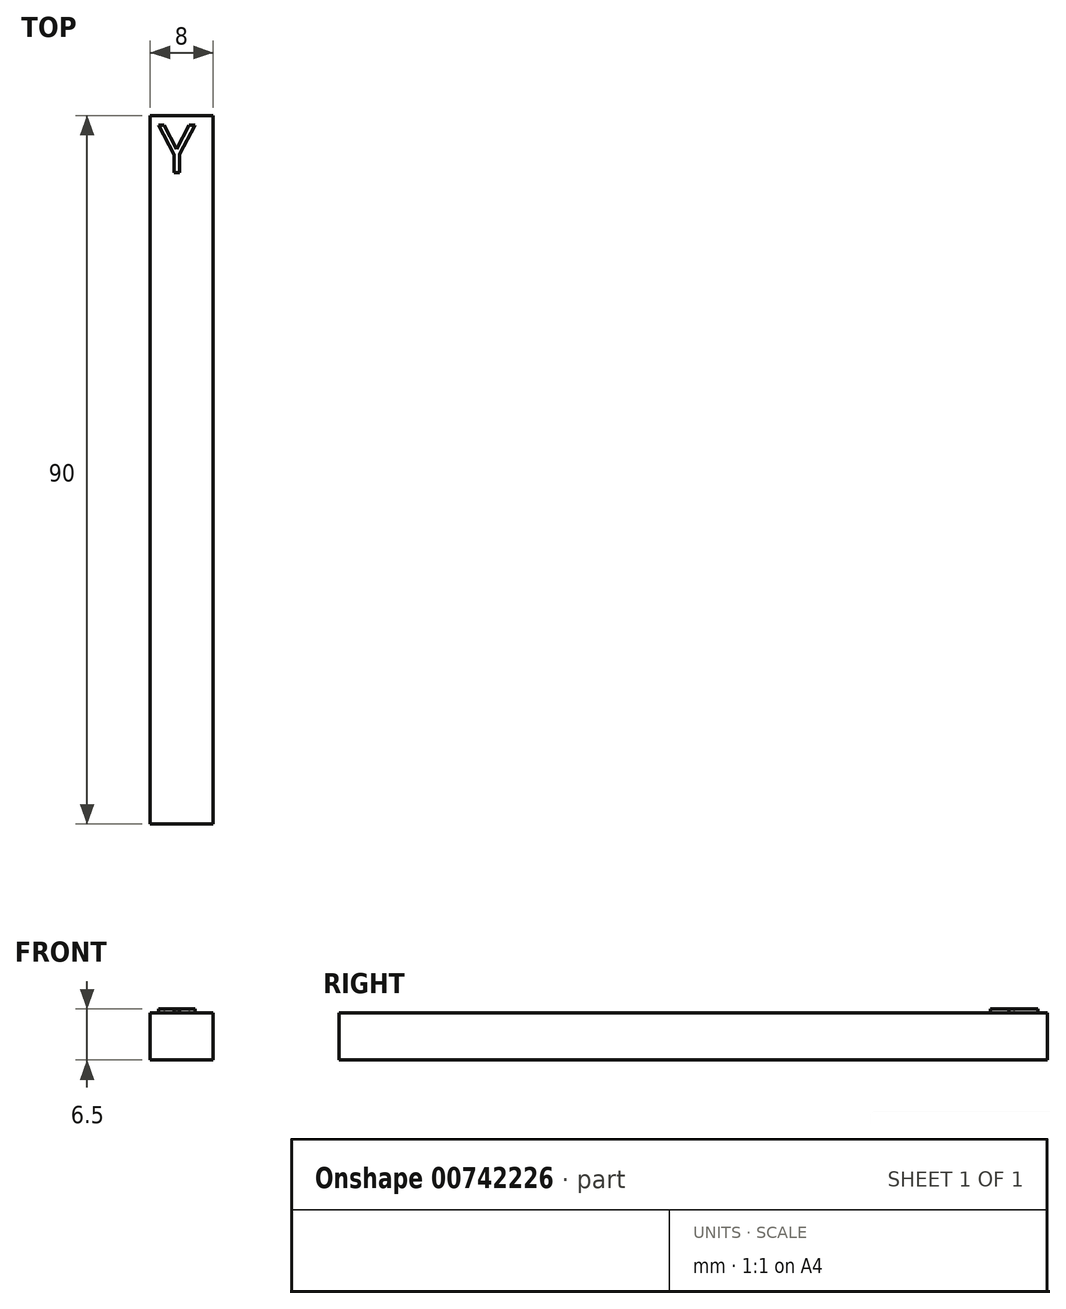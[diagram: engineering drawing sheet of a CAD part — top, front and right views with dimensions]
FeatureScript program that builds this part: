
annotation { "Feature Type Name" : "Feature", "Feature Type Description" : "" }
export const myFeature = defineFeature(function(context is Context, id is Id, definition is map)
    precondition{}
    {
        {
            var Q0;
            Q0=qCreatedBy(makeId("Front.planeOp"),FACE);
            var sketch = newSketch(context, id + "F0", { "sketchPlane" : qUnion([Q0])});
            skLineSegment(sketch, "E0.bottom", {"start": v(4, -3) * mm, "end": v(-4, -3) * mm});
            skLineSegment(sketch, "E0.top", {"start": v(4, 3) * mm, "end": v(-4, 3) * mm});
            skLineSegment(sketch, "E0.left", {"start": v(4, -3) * mm, "end": v(4, 3) * mm});
            skLineSegment(sketch, "E0.right", {"start": v(-4, -3) * mm, "end": v(-4, 3) * mm});
            skPoint(sketch, "E0.middle", {"position": v(0, 0) * mm});
            skSolve(sketch);
        }
        {
            var Q0;
            Q0=makeQuery(id+"F0.imprint","IMPRINT",FACE,{"disambiguationData":[TD([[makeQuery(id+"F0.imprint","IMPRINT",EDGE,{"derivedFrom":sQuery(id+"F0.wireOp",EDGE,"E0.bottom")}),-1.0]])]});
            extrude(context, id + "F1", {"entities" : qUnion([Q0]), "depth" : 90 * mm, "offsetDistance" : 25 * mm});
        }
        {
            var Q0;
            Q0=makeQuery(id+"F1.opExtrude","SWEPT_FACE",FACE,{"disambiguationData":[OSD([sQuery(id+"F0.wireOp",EDGE,"E0.top")])]});
            var sketch = newSketch(context, id + "F2", { "sketchPlane" : qUnion([Q0])});
            skText(sketch, "E1", { "text": "Y", "fontName": "OpenSans-Regular.ttf"});
            const initialGuessF2  = {"E1": [-0.00296, -0.00724, 1, 0, 0.00603]};
            skSetInitialGuess(sketch, initialGuessF2);
            skSolve(sketch);
        }
        {
            var Q0;
            Q0=makeQuery(id+"F2.imprint","IMPRINT",FACE,{"disambiguationData":[TD([[makeQuery(id+"F2.imprint","IMPRINT",EDGE,{"derivedFrom":sQuery(id+"F2.wireOp",EDGE,"E1.sketch_text.stroke-0")}),-1.0]])]});
            extrude(context, id + "F3", {"entities" : qUnion([Q0]), "operationType" : NewBodyOperationType.ADD, "depth" : .5 * mm, "offsetDistance" : 25 * mm});
        }
    });
